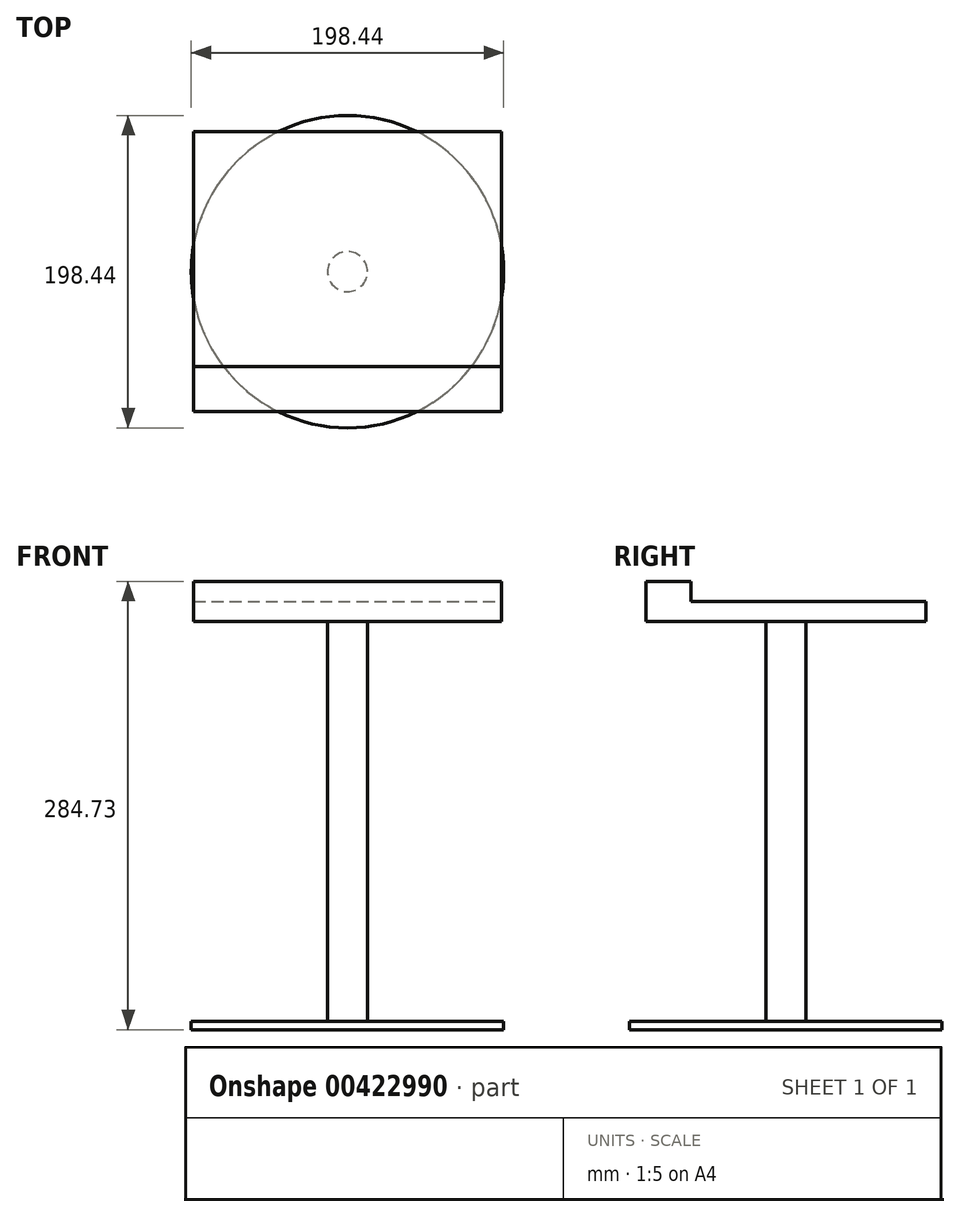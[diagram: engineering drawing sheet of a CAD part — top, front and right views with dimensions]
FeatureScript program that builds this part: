
annotation { "Feature Type Name" : "Feature", "Feature Type Description" : "" }
export const myFeature = defineFeature(function(context is Context, id is Id, definition is map)
    precondition{}
    {
        {
            var Q0;
            Q0=qCreatedBy(makeId("Top.planeOp"),FACE);
            var sketch = newSketch(context, id + "F0", { "sketchPlane" : qUnion([Q0])});
            skLineSegment(sketch, "E0.bottom", {"start": v(97.79, 88.9) * mm, "end": v(-97.8, 88.9) * mm});
            skLineSegment(sketch, "E0.top", {"start": v(97.8, -88.9) * mm, "end": v(-97.79, -88.9) * mm});
            skLineSegment(sketch, "E0.left", {"start": v(97.79, 88.9) * mm, "end": v(97.8, -88.9) * mm});
            skLineSegment(sketch, "E0.right", {"start": v(-97.8, 88.9) * mm, "end": v(-97.79, -88.9) * mm});
            skPoint(sketch, "E0.middle", {"position": v(0, 0) * mm});
            skSolve(sketch);
        }
        {
            var Q0;
            Q0 = qSketchRegion(id + "F0", true);
            extrude(context, id + "F1", {"entities" : qUnion([Q0]), "depth" : 12.7 * mm});
        }
        {
            var Q0;
            Q0=makeQuery(id+"F1.opExtrude","CAP_FACE",FACE,{"disambiguationData":[OSD([sQuery(id+"F0.wireOp",EDGE,"E0.bottom"),sQuery(id+"F0.wireOp",EDGE,"E0.top"),sQuery(id+"F0.wireOp",EDGE,"E0.left"),sQuery(id+"F0.wireOp",EDGE,"E0.right")])],"isStart":true});
            var sketch = newSketch(context, id + "F2", { "sketchPlane" : qUnion([Q0])});
            skCircle(sketch, "E1", {"center": v(0, 0) * mm, "radius": 12.7 * mm});
            skSolve(sketch);
        }
        {
            var Q0;
            Q0 = qSketchRegion(id + "F2", true);
            extrude(context, id + "F3", {"entities" : qUnion([Q0]), "operationType" : NewBodyOperationType.ADD, "depth" : 254 * mm});
        }
        {
            var Q0;
            Q0=makeQuery(id+"F3.opExtrude","CAP_FACE",FACE,{"disambiguationData":[OSD([sQuery(id+"F2.wireOp",EDGE,"E1")])],"isStart":false});
            var sketch = newSketch(context, id + "F4", { "sketchPlane" : qUnion([Q0])});
            skCircle(sketch, "E2", {"center": v(0, 0) * mm, "radius": 99.22 * mm});
            skSolve(sketch);
        }
        {
            var Q0;
            Q0 = qSketchRegion(id + "F4", true);
            extrude(context, id + "F5", {"entities" : qUnion([Q0]), "operationType" : NewBodyOperationType.ADD, "depth" : 5.33 * mm});
        }
        {
            var Q0;
            Q0=makeQuery(id+"F1.opExtrude","CAP_FACE",FACE,{"disambiguationData":[OSD([sQuery(id+"F0.wireOp",EDGE,"E0.bottom"),sQuery(id+"F0.wireOp",EDGE,"E0.top"),sQuery(id+"F0.wireOp",EDGE,"E0.left"),sQuery(id+"F0.wireOp",EDGE,"E0.right")])],"isStart":false});
            var sketch = newSketch(context, id + "F6", { "sketchPlane" : qUnion([Q0])});
            skLineSegment(sketch, "E3.bottom", {"start": v(-97.79, -88.9) * mm, "end": v(97.8, -88.9) * mm});
            skLineSegment(sketch, "E3.top", {"start": v(-97.79, -60.36) * mm, "end": v(97.8, -60.36) * mm});
            skLineSegment(sketch, "E3.left", {"start": v(-97.79, -88.9) * mm, "end": v(-97.79, -60.36) * mm});
            skLineSegment(sketch, "E3.right", {"start": v(97.8, -88.9) * mm, "end": v(97.8, -60.36) * mm});
            skSolve(sketch);
        }
        {
            var Q0;
            Q0 = qSketchRegion(id + "F6", true);
            extrude(context, id + "F7", {"entities" : qUnion([Q0]), "operationType" : NewBodyOperationType.ADD, "depth" : 12.7 * mm});
        }
    });
